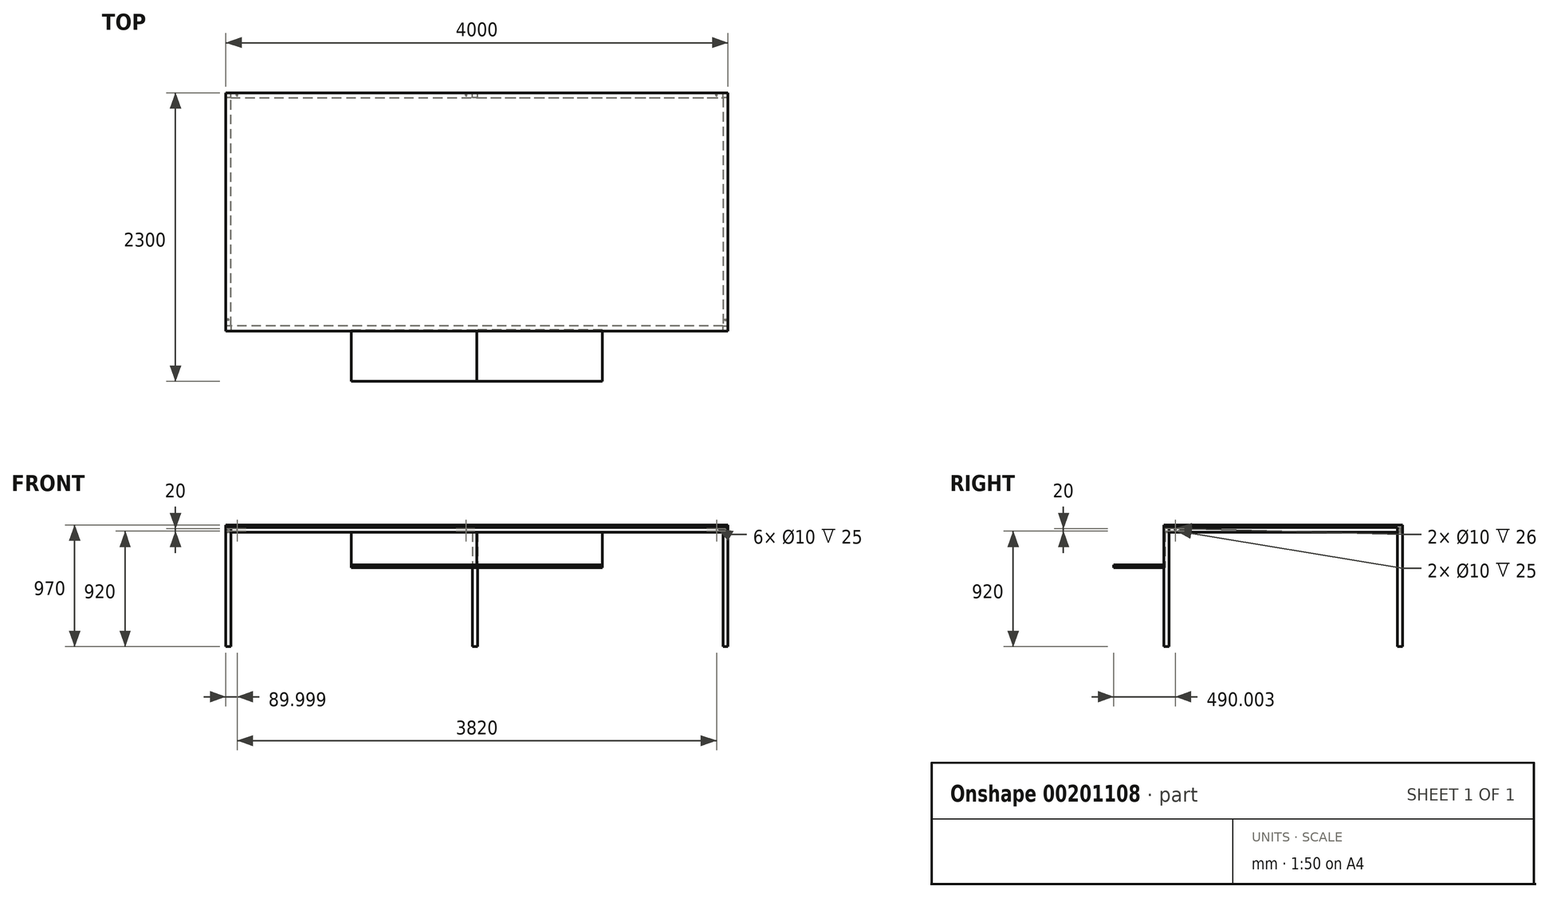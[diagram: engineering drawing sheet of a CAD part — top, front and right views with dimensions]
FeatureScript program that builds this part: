
annotation { "Feature Type Name" : "Feature", "Feature Type Description" : "" }
export const myFeature = defineFeature(function(context is Context, id is Id, definition is map)
    precondition{}
    {
        {
            var Q0;
            Q0=qCreatedBy(makeId("Top.planeOp"),FACE);
            var sketch = newSketch(context, id + "F0", { "sketchPlane" : qUnion([Q0])});
            skLineSegment(sketch, "E0.bottom", {"start": v(1995.53, -1475.08) * mm, "end": v(-2004.47, -1475.08) * mm});
            skLineSegment(sketch, "E0.top", {"start": v(1995.53, 424.92) * mm, "end": v(-2004.47, 424.92) * mm});
            skLineSegment(sketch, "E0.left", {"start": v(1995.53, -1475.08) * mm, "end": v(1995.53, 424.92) * mm});
            skLineSegment(sketch, "E0.right", {"start": v(-2004.47, -1475.08) * mm, "end": v(-2004.47, 424.92) * mm});
            skSolve(sketch);
        }
        {
            var Q0;
            Q0 = qSketchRegion(id + "F0", true);
            extrude(context, id + "F1", {"entities" : qUnion([Q0]), "endBound" : BoundingType.SYMMETRIC, "oppositeDirection" : true, "depth" : 20 * mm});
        }
        {
            var Q0;
            Q0=makeQuery(id+"F1.opExtrude","SWEPT_FACE",FACE,{"disambiguationData":[OSD([sQuery(id+"F0.wireOp",EDGE,"E0.bottom")])]});
            var sketch = newSketch(context, id + "F2", { "sketchPlane" : qUnion([Q0])});
            skLineSegment(sketch, "E1.bottom", {"start": v(-2004.47, -10) * mm, "end": v(-1964.47, -10) * mm});
            skLineSegment(sketch, "E1.top", {"start": v(-2004.47, -960) * mm, "end": v(-1964.47, -960) * mm});
            skLineSegment(sketch, "E1.left", {"start": v(-2004.47, -10) * mm, "end": v(-2004.47, -960) * mm});
            skLineSegment(sketch, "E1.right", {"start": v(-1964.47, -10) * mm, "end": v(-1964.47, -960) * mm});
            skSolve(sketch);
        }
        {
            var Q0;
            Q0 = qSketchRegion(id + "F2", true);
            extrude(context, id + "F3", {"entities" : qUnion([Q0]), "oppositeDirection" : true, "depth" : 40 * mm});
        }
        {
            var Q0;
            Q0=makeQuery(id+"F1.opExtrude","SWEPT_FACE",FACE,{"disambiguationData":[OSD([sQuery(id+"F0.wireOp",EDGE,"E0.top")])]});
            var sketch = newSketch(context, id + "F4", { "sketchPlane" : qUnion([Q0])});
            skLineSegment(sketch, "E2.bottom", {"start": v(-1995.53, -10) * mm, "end": v(-1955.53, -10) * mm});
            skLineSegment(sketch, "E2.top", {"start": v(-1995.53, -960) * mm, "end": v(-1955.53, -960) * mm});
            skLineSegment(sketch, "E2.left", {"start": v(-1995.53, -10) * mm, "end": v(-1995.53, -960) * mm});
            skLineSegment(sketch, "E2.right", {"start": v(-1955.53, -10) * mm, "end": v(-1955.53, -960) * mm});
            skSolve(sketch);
        }
        {
            var Q0;
            Q0 = qSketchRegion(id + "F4", true);
            extrude(context, id + "F5", {"entities" : qUnion([Q0]), "operationType" : NewBodyOperationType.ADD, "oppositeDirection" : true, "depth" : 40 * mm});
        }
        {
            var Q0;
            Q0=makeQuery(id+"F5.boolean.opBoolean","MERGE",FACE,{"derivedFrom":[makeQuery(id+"F1.opExtrude","SWEPT_FACE",FACE,{"disambiguationData":[OSD([sQuery(id+"F0.wireOp",EDGE,"E0.left")])]}),makeQuery(id+"F5.opExtrude","SWEPT_FACE",FACE,{"disambiguationData":[OSD([sQuery(id+"F4.wireOp",EDGE,"E2.left")])]})]});
            var sketch = newSketch(context, id + "F6", { "sketchPlane" : qUnion([Q0])});
            skLineSegment(sketch, "E3.bottom", {"start": v(-1475.08, -10) * mm, "end": v(-1435.08, -10) * mm});
            skLineSegment(sketch, "E3.top", {"start": v(-1475.08, -960) * mm, "end": v(-1435.08, -960) * mm});
            skLineSegment(sketch, "E3.left", {"start": v(-1475.08, -10) * mm, "end": v(-1475.08, -960) * mm});
            skLineSegment(sketch, "E3.right", {"start": v(-1435.08, -10) * mm, "end": v(-1435.08, -960) * mm});
            skSolve(sketch);
        }
        {
            var Q0;
            Q0 = qSketchRegion(id + "F6", true);
            extrude(context, id + "F7", {"entities" : qUnion([Q0]), "oppositeDirection" : true, "depth" : 40 * mm});
        }
        {
            var Q0;
            Q0=makeQuery(id+"F5.boolean.opBoolean","MERGE",FACE,{"derivedFrom":[makeQuery(id+"F1.opExtrude","SWEPT_FACE",FACE,{"disambiguationData":[OSD([sQuery(id+"F0.wireOp",EDGE,"E0.top")])]}),makeQuery(id+"F5.opExtrude","CAP_FACE",FACE,{"disambiguationData":[OSD([sQuery(id+"F4.wireOp",EDGE,"E2.bottom"),sQuery(id+"F4.wireOp",EDGE,"E2.top"),sQuery(id+"F4.wireOp",EDGE,"E2.left"),sQuery(id+"F4.wireOp",EDGE,"E2.right")])],"isStart":true})]});
            var sketch = newSketch(context, id + "F8", { "sketchPlane" : qUnion([Q0])});
            skLineSegment(sketch, "E4.bottom", {"start": v(2004.47, -10) * mm, "end": v(1964.47, -10) * mm});
            skLineSegment(sketch, "E4.top", {"start": v(2004.47, -960) * mm, "end": v(1964.47, -960) * mm});
            skLineSegment(sketch, "E4.left", {"start": v(2004.47, -10) * mm, "end": v(2004.47, -960) * mm});
            skLineSegment(sketch, "E4.right", {"start": v(1964.47, -10) * mm, "end": v(1964.47, -960) * mm});
            skSolve(sketch);
        }
        {
            var Q0;
            Q0 = qSketchRegion(id + "F8", true);
            extrude(context, id + "F9", {"entities" : qUnion([Q0]), "oppositeDirection" : true, "depth" : 40 * mm});
        }
        {
            var Q0;
            Q0=makeQuery(id+"F3.opExtrude","SWEPT_FACE",FACE,{"disambiguationData":[OSD([sQuery(id+"F2.wireOp",EDGE,"E1.right")])]});
            var sketch = newSketch(context, id + "F10", { "sketchPlane" : qUnion([Q0])});
            skLineSegment(sketch, "E5.bottom", {"start": v(-1475.08, -10) * mm, "end": v(-1435.08, -10) * mm});
            skLineSegment(sketch, "E5.top", {"start": v(-1475.08, -50) * mm, "end": v(-1435.08, -50) * mm});
            skLineSegment(sketch, "E5.left", {"start": v(-1475.08, -10) * mm, "end": v(-1475.08, -50) * mm});
            skLineSegment(sketch, "E5.right", {"start": v(-1435.08, -10) * mm, "end": v(-1435.08, -50) * mm});
            skSolve(sketch);
        }
        {
            var Q0;
            Q0 = qSketchRegion(id + "F10", true);
            extrude(context, id + "F11", {"entities" : qUnion([Q0]), "endBound" : BoundingType.UP_TO_NEXT, "depth" : 25.4 * mm});
        }
        {
            var Q0;
            Q0=makeQuery(id+"F5.opExtrude","SWEPT_FACE",FACE,{"disambiguationData":[OSD([sQuery(id+"F4.wireOp",EDGE,"E2.right")])]});
            var sketch = newSketch(context, id + "F12", { "sketchPlane" : qUnion([Q0])});
            skLineSegment(sketch, "E6.bottom", {"start": v(-424.92, -10) * mm, "end": v(-384.92, -10) * mm});
            skLineSegment(sketch, "E6.top", {"start": v(-424.92, -50) * mm, "end": v(-384.92, -50) * mm});
            skLineSegment(sketch, "E6.left", {"start": v(-424.92, -10) * mm, "end": v(-424.92, -50) * mm});
            skLineSegment(sketch, "E6.right", {"start": v(-384.92, -10) * mm, "end": v(-384.92, -50) * mm});
            skSolve(sketch);
        }
        {
            var Q0;
            Q0 = qSketchRegion(id + "F12", true);
            extrude(context, id + "F13", {"entities" : qUnion([Q0]), "endBound" : BoundingType.UP_TO_NEXT, "depth" : 25.4 * mm});
        }
        {
            var Q0;
            Q0=makeQuery(id+"F9.opExtrude","CAP_FACE",FACE,{"disambiguationData":[OSD([sQuery(id+"F8.wireOp",EDGE,"E4.bottom"),sQuery(id+"F8.wireOp",EDGE,"E4.top"),sQuery(id+"F8.wireOp",EDGE,"E4.left"),sQuery(id+"F8.wireOp",EDGE,"E4.right")])],"isStart":false});
            var sketch = newSketch(context, id + "F14", { "sketchPlane" : qUnion([Q0])});
            skLineSegment(sketch, "E7.bottom", {"start": v(-2004.47, -10) * mm, "end": v(-1964.47, -10) * mm});
            skLineSegment(sketch, "E7.top", {"start": v(-2004.47, -50) * mm, "end": v(-1964.47, -50) * mm});
            skLineSegment(sketch, "E7.left", {"start": v(-2004.47, -10) * mm, "end": v(-2004.47, -50) * mm});
            skLineSegment(sketch, "E7.right", {"start": v(-1964.47, -10) * mm, "end": v(-1964.47, -50) * mm});
            skSolve(sketch);
        }
        {
            var Q0;
            Q0 = qSketchRegion(id + "F14", true);
            extrude(context, id + "F15", {"entities" : qUnion([Q0]), "endBound" : BoundingType.UP_TO_NEXT, "depth" : 25.4 * mm});
        }
        {
            var Q0;
            Q0=makeQuery(id+"F7.opExtrude","SWEPT_FACE",FACE,{"disambiguationData":[OSD([sQuery(id+"F6.wireOp",EDGE,"E3.right")])]});
            var sketch = newSketch(context, id + "F16", { "sketchPlane" : qUnion([Q0])});
            skLineSegment(sketch, "E8.bottom", {"start": v(-1995.53, -10) * mm, "end": v(-1955.53, -10) * mm});
            skLineSegment(sketch, "E8.top", {"start": v(-1995.53, -50) * mm, "end": v(-1955.53, -50) * mm});
            skLineSegment(sketch, "E8.left", {"start": v(-1995.53, -10) * mm, "end": v(-1995.53, -50) * mm});
            skLineSegment(sketch, "E8.right", {"start": v(-1955.53, -10) * mm, "end": v(-1955.53, -50) * mm});
            skSolve(sketch);
        }
        {
            var Q0;
            Q0 = qSketchRegion(id + "F16", true);
            extrude(context, id + "F17", {"entities" : qUnion([Q0]), "endBound" : BoundingType.UP_TO_NEXT, "depth" : 25.4 * mm});
        }
        {
            var Q0;
            Q0=makeQuery(id+"F11.opExtrude","SWEPT_FACE",FACE,{"disambiguationData":[OSD([sQuery(id+"F10.wireOp",EDGE,"E5.left")])]});
            var sketch = newSketch(context, id + "F18", { "sketchPlane" : qUnion([Q0])});
            skLineSegment(sketch, "E9.bottom", {"start": v(-4.47, -50) * mm, "end": v(995.53, -50) * mm});
            skLineSegment(sketch, "E9.top", {"start": v(-4.47, -310) * mm, "end": v(995.53, -310) * mm});
            skLineSegment(sketch, "E9.left", {"start": v(-4.47, -50) * mm, "end": v(-4.47, -310) * mm});
            skLineSegment(sketch, "E9.right", {"start": v(995.53, -50) * mm, "end": v(995.53, -310) * mm});
            skSolve(sketch);
        }
        {
            var Q0;
            Q0 = qSketchRegion(id + "F18", true);
            extrude(context, id + "F19", {"entities" : qUnion([Q0]), "operationType" : NewBodyOperationType.ADD, "oppositeDirection" : true, "depth" : 10 * mm});
        }
        {
            var Q0;
            Q0=makeQuery(id+"F13.opExtrude","SWEPT_FACE",FACE,{"disambiguationData":[OSD([sQuery(id+"F12.wireOp",EDGE,"E6.left")])]});
            var sketch = newSketch(context, id + "F20", { "sketchPlane" : qUnion([Q0])});
            skLineSegment(sketch, "E10.bottom", {"start": v(0, -50) * mm, "end": v(40, -50) * mm});
            skLineSegment(sketch, "E10.top", {"start": v(0, -960) * mm, "end": v(40, -960) * mm});
            skLineSegment(sketch, "E10.left", {"start": v(0, -50) * mm, "end": v(0, -960) * mm});
            skLineSegment(sketch, "E10.right", {"start": v(40, -50) * mm, "end": v(40, -960) * mm});
            skSolve(sketch);
        }
        {
            var Q0;
            Q0 = qSketchRegion(id + "F20", true);
            extrude(context, id + "F21", {"entities" : qUnion([Q0]), "operationType" : NewBodyOperationType.ADD, "oppositeDirection" : true, "depth" : 40 * mm});
        }
        {
            var Q0;
            Q0=makeQuery(id+"F19.opExtrude","CAP_FACE",FACE,{"disambiguationData":[OSD([sQuery(id+"F18.wireOp",EDGE,"E9.bottom"),sQuery(id+"F18.wireOp",EDGE,"E9.top"),sQuery(id+"F18.wireOp",EDGE,"E9.left"),sQuery(id+"F18.wireOp",EDGE,"E9.right")])],"isStart":false});
            var sketch = newSketch(context, id + "F22", { "sketchPlane" : qUnion([Q0])});
            skLineSegment(sketch, "E11.bottom", {"start": v(-995.53, -310) * mm, "end": v(4.47, -310) * mm});
            skLineSegment(sketch, "E11.top", {"start": v(-995.53, -332) * mm, "end": v(4.47, -332) * mm});
            skLineSegment(sketch, "E11.left", {"start": v(-995.53, -310) * mm, "end": v(-995.53, -332) * mm});
            skLineSegment(sketch, "E11.right", {"start": v(4.47, -310) * mm, "end": v(4.47, -332) * mm});
            skSolve(sketch);
        }
        {
            var Q0;
            Q0 = qSketchRegion(id + "F22", true);
            extrude(context, id + "F23", {"entities" : qUnion([Q0]), "operationType" : NewBodyOperationType.ADD, "oppositeDirection" : true, "depth" : 410 * mm});
        }
        {
            var Q0;
            Q0=makeQuery(id+"F11.opExtrude","SWEPT_BODY",BODY,{"disambiguationData":[OSD([sQuery(id+"F10.wireOp",EDGE,"E5.bottom"),sQuery(id+"F10.wireOp",EDGE,"E5.top"),sQuery(id+"F10.wireOp",EDGE,"E5.left"),sQuery(id+"F10.wireOp",EDGE,"E5.right")])]});
            var Q1;
            Q1=makeQuery(id+"F23.boolean.opBoolean","MERGE",FACE,{"derivedFrom":[makeQuery(id+"F19.opExtrude","SWEPT_FACE",FACE,{"disambiguationData":[OSD([sQuery(id+"F18.wireOp",EDGE,"E9.left")])]}),makeQuery(id+"F23.opExtrude","SWEPT_FACE",FACE,{"disambiguationData":[OSD([sQuery(id+"F22.wireOp",EDGE,"E11.right")])]})]});
            mirror(context, id + "F24", {"entities" : qUnion([Q0]), "mirrorPlane" : qUnion([Q1])});
        }
        {
            var Q0;
            Q0=makeQuery(id+"F17.opExtrude","SWEPT_FACE",FACE,{"disambiguationData":[OSD([sQuery(id+"F16.wireOp",EDGE,"E8.left")])]});
            var sketch = newSketch(context, id + "F25", { "sketchPlane" : qUnion([Q0])});
            skCircle(sketch, "E12", {"center": v(-1385.08, -20) * mm, "radius": 5 * mm});
            skCircle(sketch, "E13", {"center": v(-1385.08, -40) * mm, "radius": 5 * mm});
            skSolve(sketch);
        }
        {
            var Q0;
            Q0 = qSketchRegion(id + "F25", true);
            extrude(context, id + "F26", {"entities" : qUnion([Q0]), "operationType" : NewBodyOperationType.REMOVE, "oppositeDirection" : true, "depth" : 26 * mm});
        }
        {
            var Q0;
            Q0=makeQuery(id+"F15.opExtrude","SWEPT_FACE",FACE,{"disambiguationData":[OSD([sQuery(id+"F14.wireOp",EDGE,"E7.left")])]});
            var sketch = newSketch(context, id + "F27", { "sketchPlane" : qUnion([Q0])});
            skCircle(sketch, "E14", {"center": v(1385.08, -20) * mm, "radius": 5 * mm});
            skCircle(sketch, "E15", {"center": v(1385.08, -40) * mm, "radius": 5 * mm});
            skSolve(sketch);
        }
        {
            var Q0;
            Q0 = qSketchRegion(id + "F27", true);
            extrude(context, id + "F28", {"entities" : qUnion([Q0]), "operationType" : NewBodyOperationType.REMOVE, "oppositeDirection" : true, "depth" : 25 * mm});
        }
        {
            var Q0;
            Q0=makeQuery(id+"F21.boolean.opBoolean","MERGE",FACE,{"derivedFrom":[makeQuery(id+"F13.opExtrude","SWEPT_FACE",FACE,{"disambiguationData":[OSD([sQuery(id+"F12.wireOp",EDGE,"E6.left")])]}),makeQuery(id+"F21.opExtrude","CAP_FACE",FACE,{"disambiguationData":[OSD([sQuery(id+"F20.wireOp",EDGE,"E10.bottom"),sQuery(id+"F20.wireOp",EDGE,"E10.top"),sQuery(id+"F20.wireOp",EDGE,"E10.left"),sQuery(id+"F20.wireOp",EDGE,"E10.right")])],"isStart":true})]});
            var sketch = newSketch(context, id + "F29", { "sketchPlane" : qUnion([Q0])});
            skCircle(sketch, "E16", {"center": v(1914.47, -20) * mm, "radius": 5 * mm});
            skCircle(sketch, "E17", {"center": v(1914.47, -40) * mm, "radius": 5 * mm});
            skSolve(sketch);
        }
        {
            var Q0;
            Q0 = qSketchRegion(id + "F29", true);
            extrude(context, id + "F30", {"entities" : qUnion([Q0]), "operationType" : NewBodyOperationType.REMOVE, "oppositeDirection" : true, "depth" : 25 * mm});
        }
        {
            var Q0;
            Q0=makeQuery(id+"F21.boolean.opBoolean","MERGE",FACE,{"derivedFrom":[makeQuery(id+"F13.opExtrude","SWEPT_FACE",FACE,{"disambiguationData":[OSD([sQuery(id+"F12.wireOp",EDGE,"E6.left")])]}),makeQuery(id+"F21.opExtrude","CAP_FACE",FACE,{"disambiguationData":[OSD([sQuery(id+"F20.wireOp",EDGE,"E10.bottom"),sQuery(id+"F20.wireOp",EDGE,"E10.top"),sQuery(id+"F20.wireOp",EDGE,"E10.left"),sQuery(id+"F20.wireOp",EDGE,"E10.right")])],"isStart":true})]});
            var sketch = newSketch(context, id + "F31", { "sketchPlane" : qUnion([Q0])});
            skCircle(sketch, "E18", {"center": v(90, -20) * mm, "radius": 5 * mm});
            skCircle(sketch, "E19", {"center": v(90, -40) * mm, "radius": 5 * mm});
            skSolve(sketch);
        }
        {
            var Q0;
            Q0 = qSketchRegion(id + "F31", true);
            extrude(context, id + "F32", {"entities" : qUnion([Q0]), "operationType" : NewBodyOperationType.REMOVE, "oppositeDirection" : true, "depth" : 25 * mm});
        }
        {
            var Q0;
            Q0=makeQuery(id+"F21.boolean.opBoolean","MERGE",FACE,{"derivedFrom":[makeQuery(id+"F13.opExtrude","SWEPT_FACE",FACE,{"disambiguationData":[OSD([sQuery(id+"F12.wireOp",EDGE,"E6.left")])]}),makeQuery(id+"F21.opExtrude","CAP_FACE",FACE,{"disambiguationData":[OSD([sQuery(id+"F20.wireOp",EDGE,"E10.bottom"),sQuery(id+"F20.wireOp",EDGE,"E10.top"),sQuery(id+"F20.wireOp",EDGE,"E10.left"),sQuery(id+"F20.wireOp",EDGE,"E10.right")])],"isStart":true})]});
            var sketch = newSketch(context, id + "F33", { "sketchPlane" : qUnion([Q0])});
            skCircle(sketch, "E20", {"center": v(-1905.53, -20) * mm, "radius": 5 * mm});
            skCircle(sketch, "E21", {"center": v(-1905.53, -40) * mm, "radius": 5 * mm});
            skSolve(sketch);
        }
        {
            var Q0;
            Q0 = qSketchRegion(id + "F33", true);
            extrude(context, id + "F34", {"entities" : qUnion([Q0]), "operationType" : NewBodyOperationType.REMOVE, "oppositeDirection" : true, "depth" : 25 * mm});
        }
    });
